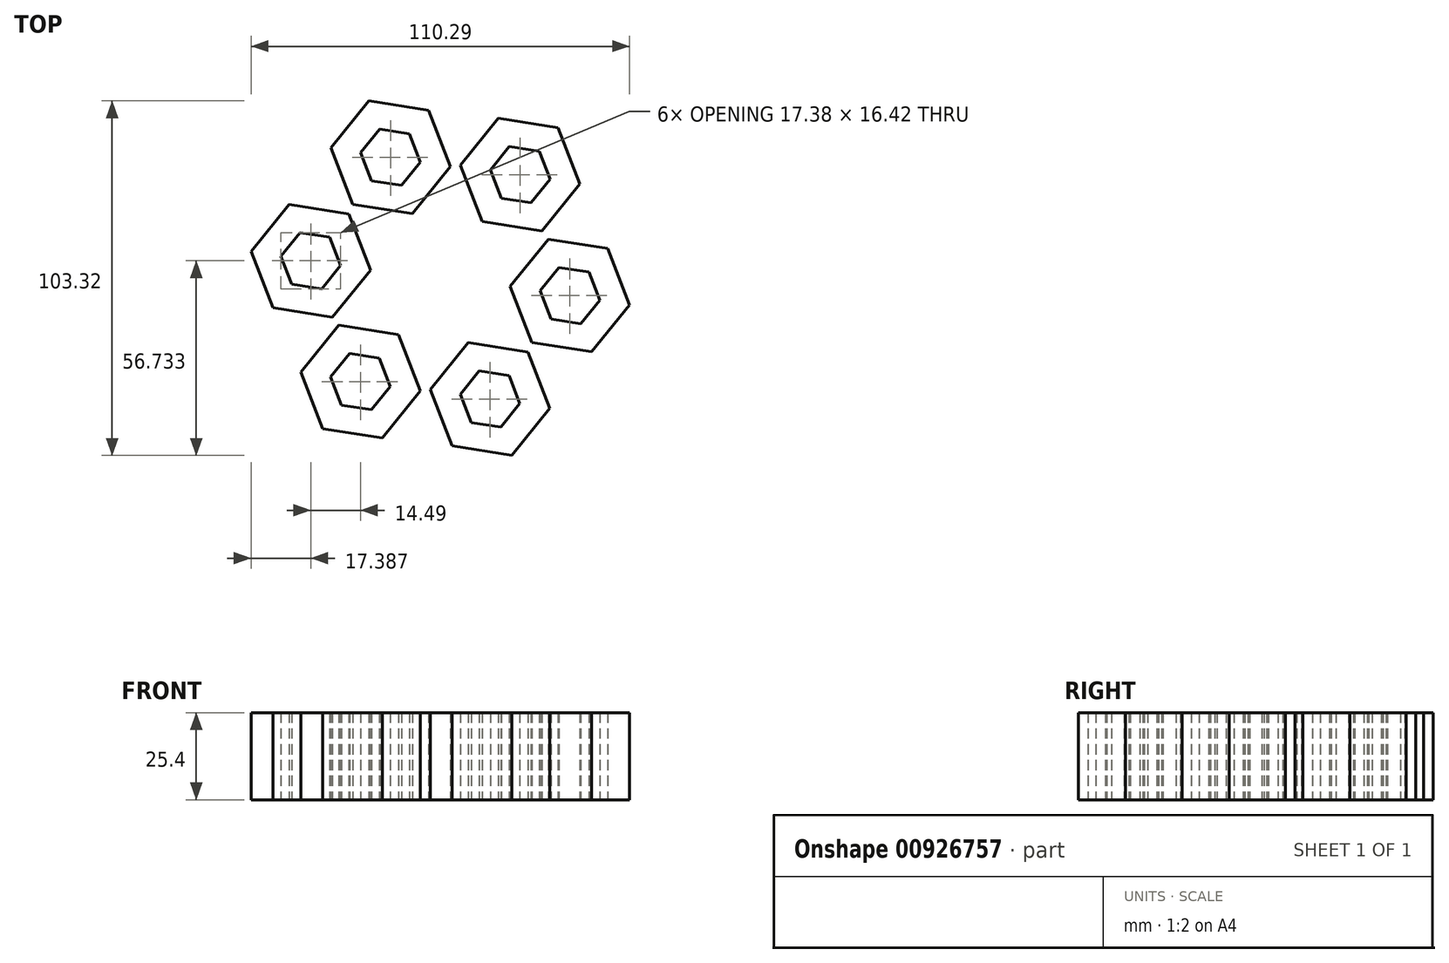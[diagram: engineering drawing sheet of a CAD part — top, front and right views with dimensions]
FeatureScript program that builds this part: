
annotation { "Feature Type Name" : "Feature", "Feature Type Description" : "" }
export const myFeature = defineFeature(function(context is Context, id is Id, definition is map)
    precondition{}
    {
        {
            var Q0;
            Q0=qCreatedBy(makeId("Top.planeOp"),FACE);
            var sketch = newSketch(context, id + "F0", { "sketchPlane" : qUnion([Q0])});
            skCircle(sketch, "E0.cCircle", {"center": v(0, 0) * mm, "radius": 15.24 * mm, "construction": true});
            skLineSegment(sketch, "E0.0", {"start": v(-17.38, 2.73) * mm, "end": v(-6.32, 16.42) * mm});
            skLineSegment(sketch, "E0.1", {"start": v(-6.32, 16.42) * mm, "end": v(11.06, 13.69) * mm});
            skLineSegment(sketch, "E0.2", {"start": v(11.06, 13.69) * mm, "end": v(17.38, -2.73) * mm});
            skLineSegment(sketch, "E0.3", {"start": v(17.38, -2.73) * mm, "end": v(6.32, -16.42) * mm});
            skLineSegment(sketch, "E0.4", {"start": v(6.32, -16.42) * mm, "end": v(-11.06, -13.69) * mm});
            skLineSegment(sketch, "E0.5", {"start": v(-11.06, -13.69) * mm, "end": v(-17.38, 2.73) * mm});
            skPoint(sketch, "E0.0.midPoint", {"position": v(-11.85, 9.58) * mm});
            skLineSegment(sketch, "E1", {"start": v(0, 0) * mm, "end": v(-23.27, -30.17) * mm});
            skLineSegment(sketch, "E2.1.0", {"start": v(-48.82, -8.62) * mm, "end": v(-55.15, 7.8) * mm});
            skLineSegment(sketch, "E2.1.1", {"start": v(-55.15, 7.8) * mm, "end": v(-44.09, 21.5) * mm});
            skLineSegment(sketch, "E2.1.2", {"start": v(-44.09, 21.5) * mm, "end": v(-26.7, 18.76) * mm});
            skLineSegment(sketch, "E2.1.3", {"start": v(-26.7, 18.76) * mm, "end": v(-20.38, 2.34) * mm});
            skLineSegment(sketch, "E2.1.4", {"start": v(-20.38, 2.34) * mm, "end": v(-31.44, -11.35) * mm});
            skLineSegment(sketch, "E2.1.5", {"start": v(-31.44, -11.35) * mm, "end": v(-48.82, -8.62) * mm});
            skLineSegment(sketch, "E2.2.0", {"start": v(-54.7, -41.52) * mm, "end": v(-72.1, -38.78) * mm});
            skLineSegment(sketch, "E2.2.1", {"start": v(-72.1, -38.78) * mm, "end": v(-78.42, -22.36) * mm});
            skLineSegment(sketch, "E2.2.2", {"start": v(-78.42, -22.36) * mm, "end": v(-67.36, -8.67) * mm});
            skLineSegment(sketch, "E2.2.3", {"start": v(-67.36, -8.67) * mm, "end": v(-49.97, -11.4) * mm});
            skLineSegment(sketch, "E2.2.4", {"start": v(-49.97, -11.4) * mm, "end": v(-43.65, -27.83) * mm});
            skLineSegment(sketch, "E2.2.5", {"start": v(-43.65, -27.83) * mm, "end": v(-54.7, -41.52) * mm});
            skLineSegment(sketch, "E2.3.0", {"start": v(-29.16, -63.07) * mm, "end": v(-40.22, -76.76) * mm});
            skLineSegment(sketch, "E2.3.1", {"start": v(-40.22, -76.76) * mm, "end": v(-57.6, -74.02) * mm});
            skLineSegment(sketch, "E2.3.2", {"start": v(-57.6, -74.02) * mm, "end": v(-63.93, -57.6) * mm});
            skLineSegment(sketch, "E2.3.3", {"start": v(-63.93, -57.6) * mm, "end": v(-52.87, -43.91) * mm});
            skLineSegment(sketch, "E2.3.4", {"start": v(-52.87, -43.91) * mm, "end": v(-35.48, -46.65) * mm});
            skLineSegment(sketch, "E2.3.5", {"start": v(-35.48, -46.65) * mm, "end": v(-29.16, -63.07) * mm});
            skLineSegment(sketch, "E2.4.0", {"start": v(2.28, -51.72) * mm, "end": v(8.6, -68.14) * mm});
            skLineSegment(sketch, "E2.4.1", {"start": v(8.6, -68.14) * mm, "end": v(-2.46, -81.83) * mm});
            skLineSegment(sketch, "E2.4.2", {"start": v(-2.46, -81.83) * mm, "end": v(-19.84, -79.1) * mm});
            skLineSegment(sketch, "E2.4.3", {"start": v(-19.84, -79.1) * mm, "end": v(-26.17, -62.67) * mm});
            skLineSegment(sketch, "E2.4.4", {"start": v(-26.17, -62.67) * mm, "end": v(-15.1, -48.98) * mm});
            skLineSegment(sketch, "E2.4.5", {"start": v(-15.1, -48.98) * mm, "end": v(2.28, -51.72) * mm});
            skLineSegment(sketch, "E2.5.0", {"start": v(8.17, -18.82) * mm, "end": v(25.55, -21.55) * mm});
            skLineSegment(sketch, "E2.5.1", {"start": v(25.55, -21.55) * mm, "end": v(31.87, -37.97) * mm});
            skLineSegment(sketch, "E2.5.2", {"start": v(31.87, -37.97) * mm, "end": v(20.81, -51.66) * mm});
            skLineSegment(sketch, "E2.5.3", {"start": v(20.81, -51.66) * mm, "end": v(3.43, -48.93) * mm});
            skLineSegment(sketch, "E2.5.4", {"start": v(3.43, -48.93) * mm, "end": v(-2.9, -32.5) * mm});
            skLineSegment(sketch, "E2.5.5", {"start": v(-2.9, -32.5) * mm, "end": v(8.17, -18.82) * mm});
            skPoint(sketch, "E2.center", {"position": v(-23.27, -30.17) * mm});
            skLineSegment(sketch, "E3", {"start": v(0, 0) * mm, "end": v(-2.37, -15.05) * mm});
            skCircle(sketch, "E4.cCircle", {"center": v(0, 0) * mm, "radius": 7.62 * mm, "construction": true});
            skLineSegment(sketch, "E4.0", {"start": v(3.16, -8.21) * mm, "end": v(-5.53, -6.84) * mm});
            skLineSegment(sketch, "E4.1", {"start": v(-5.53, -6.84) * mm, "end": v(-8.7, 1.37) * mm});
            skLineSegment(sketch, "E4.2", {"start": v(-8.7, 1.37) * mm, "end": v(-3.16, 8.21) * mm});
            skLineSegment(sketch, "E4.3", {"start": v(-3.16, 8.21) * mm, "end": v(5.53, 6.84) * mm});
            skLineSegment(sketch, "E4.4", {"start": v(5.53, 6.84) * mm, "end": v(8.7, -1.37) * mm});
            skLineSegment(sketch, "E4.5", {"start": v(8.7, -1.37) * mm, "end": v(3.16, -8.21) * mm});
            skPoint(sketch, "E4.0.midPoint", {"position": v(-1.18, -7.53) * mm});
            skLineSegment(sketch, "E5.1.0", {"start": v(-34.6, -3.14) * mm, "end": v(-43.3, -1.77) * mm});
            skLineSegment(sketch, "E5.1.1", {"start": v(-43.3, -1.77) * mm, "end": v(-46.45, 6.44) * mm});
            skLineSegment(sketch, "E5.1.2", {"start": v(-46.45, 6.44) * mm, "end": v(-40.92, 13.28) * mm});
            skLineSegment(sketch, "E5.1.3", {"start": v(-40.92, 13.28) * mm, "end": v(-32.23, 11.91) * mm});
            skLineSegment(sketch, "E5.1.4", {"start": v(-32.23, 11.91) * mm, "end": v(-29.07, 3.7) * mm});
            skLineSegment(sketch, "E5.1.5", {"start": v(-29.07, 3.7) * mm, "end": v(-34.6, -3.14) * mm});
            skLineSegment(sketch, "E5.2.0", {"start": v(-52.34, -26.46) * mm, "end": v(-57.87, -33.3) * mm});
            skLineSegment(sketch, "E5.2.1", {"start": v(-57.87, -33.3) * mm, "end": v(-66.56, -31.94) * mm});
            skLineSegment(sketch, "E5.2.2", {"start": v(-66.56, -31.94) * mm, "end": v(-69.72, -23.73) * mm});
            skLineSegment(sketch, "E5.2.3", {"start": v(-69.72, -23.73) * mm, "end": v(-64.2, -16.89) * mm});
            skLineSegment(sketch, "E5.2.4", {"start": v(-64.2, -16.89) * mm, "end": v(-55.5, -18.25) * mm});
            skLineSegment(sketch, "E5.2.5", {"start": v(-55.5, -18.25) * mm, "end": v(-52.34, -26.46) * mm});
            skLineSegment(sketch, "E5.3.0", {"start": v(-41.01, -53.5) * mm, "end": v(-37.85, -61.7) * mm});
            skLineSegment(sketch, "E5.3.1", {"start": v(-37.85, -61.7) * mm, "end": v(-43.38, -68.55) * mm});
            skLineSegment(sketch, "E5.3.2", {"start": v(-43.38, -68.55) * mm, "end": v(-52.07, -67.18) * mm});
            skLineSegment(sketch, "E5.3.3", {"start": v(-52.07, -67.18) * mm, "end": v(-55.23, -58.97) * mm});
            skLineSegment(sketch, "E5.3.4", {"start": v(-55.23, -58.97) * mm, "end": v(-49.7, -52.12) * mm});
            skLineSegment(sketch, "E5.3.5", {"start": v(-49.7, -52.12) * mm, "end": v(-41.01, -53.5) * mm});
            skLineSegment(sketch, "E5.4.0", {"start": v(-11.94, -57.2) * mm, "end": v(-3.25, -58.56) * mm});
            skLineSegment(sketch, "E5.4.1", {"start": v(-3.25, -58.56) * mm, "end": v(-0.09, -66.77) * mm});
            skLineSegment(sketch, "E5.4.2", {"start": v(-0.09, -66.77) * mm, "end": v(-5.62, -73.62) * mm});
            skLineSegment(sketch, "E5.4.3", {"start": v(-5.62, -73.62) * mm, "end": v(-14.31, -72.25) * mm});
            skLineSegment(sketch, "E5.4.4", {"start": v(-14.31, -72.25) * mm, "end": v(-17.47, -64.04) * mm});
            skLineSegment(sketch, "E5.4.5", {"start": v(-17.47, -64.04) * mm, "end": v(-11.94, -57.2) * mm});
            skLineSegment(sketch, "E5.5.0", {"start": v(5.8, -33.87) * mm, "end": v(11.33, -27.03) * mm});
            skLineSegment(sketch, "E5.5.1", {"start": v(11.33, -27.03) * mm, "end": v(20.02, -28.4) * mm});
            skLineSegment(sketch, "E5.5.2", {"start": v(20.02, -28.4) * mm, "end": v(23.18, -36.6) * mm});
            skLineSegment(sketch, "E5.5.3", {"start": v(23.18, -36.6) * mm, "end": v(17.65, -43.45) * mm});
            skLineSegment(sketch, "E5.5.4", {"start": v(17.65, -43.45) * mm, "end": v(8.96, -42.08) * mm});
            skLineSegment(sketch, "E5.5.5", {"start": v(8.96, -42.08) * mm, "end": v(5.8, -33.87) * mm});
            skSolve(sketch);
        }
        {
            var Q0;
            Q0=makeQuery(id+"F0.imprint","IMPRINT",FACE,{"disambiguationData":[TD([[makeQuery(id+"F0.imprint","IMPRINT",EDGE,{"derivedFrom":sQuery(id+"F0.wireOp",EDGE,"E2.2.0")}),-1.0]])]});
            var Q1;
            Q1=makeQuery(id+"F0.imprint","IMPRINT",FACE,{"disambiguationData":[TD([[makeQuery(id+"F0.imprint","IMPRINT",EDGE,{"derivedFrom":sQuery(id+"F0.wireOp",EDGE,"E2.1.0")}),-1.0]])]});
            var Q2;
            {var subQ0=sQuery(id+"F0.wireOp",EDGE,"E3");var subQ1=sQuery(id+"F0.wireOp",EDGE,"E0.4");var subQ2=makeQuery(id+"F0.imprint","INTERSECT",VERTEX,{"derivedFrom":[subQ1,subQ0]});Q2=makeQuery(id+"F0.imprint","IMPRINT",FACE,{"disambiguationData":[TD([[makeQuery(id+"F0.imprint","IMPRINT",EDGE,{"disambiguationData":[TD([[subQ2,-1.0]])],"derivedFrom":subQ1}),-1.0]])]});}
            var Q3;
            Q3=makeQuery(id+"F0.imprint","IMPRINT",FACE,{"disambiguationData":[TD([[makeQuery(id+"F0.imprint","IMPRINT",EDGE,{"derivedFrom":sQuery(id+"F0.wireOp",EDGE,"E0.0")}),-1.0]])]});
            var Q4;
            Q4=makeQuery(id+"F0.imprint","IMPRINT",FACE,{"disambiguationData":[TD([[makeQuery(id+"F0.imprint","IMPRINT",EDGE,{"derivedFrom":sQuery(id+"F0.wireOp",EDGE,"E2.5.0")}),-1.0]])]});
            var Q5;
            Q5=makeQuery(id+"F0.imprint","IMPRINT",FACE,{"disambiguationData":[TD([[makeQuery(id+"F0.imprint","IMPRINT",EDGE,{"derivedFrom":sQuery(id+"F0.wireOp",EDGE,"E2.4.0")}),-1.0]])]});
            var Q6;
            Q6=makeQuery(id+"F0.imprint","IMPRINT",FACE,{"disambiguationData":[TD([[makeQuery(id+"F0.imprint","IMPRINT",EDGE,{"derivedFrom":sQuery(id+"F0.wireOp",EDGE,"E2.3.0")}),-1.0]])]});
            extrude(context, id + "F1", {"entities" : qUnion([Q0, Q1, Q2, Q3, Q4, Q5, Q6]), "depth" : 25.4 * mm, "offsetDistance" : 25.4 * mm});
        }
    });
